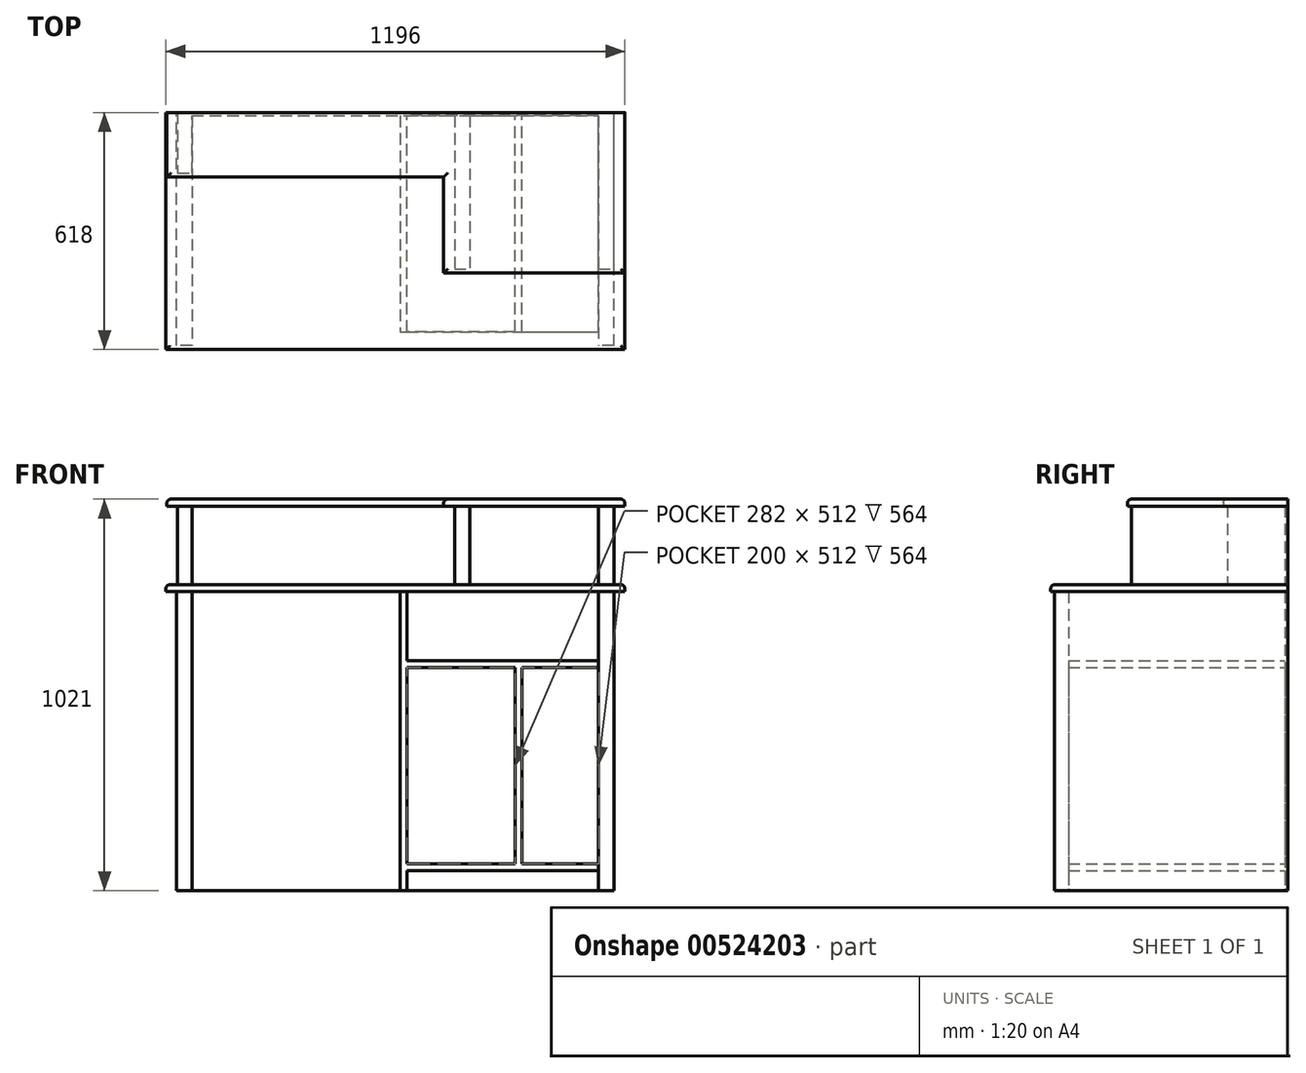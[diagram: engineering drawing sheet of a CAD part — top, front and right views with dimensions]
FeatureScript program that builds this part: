
annotation { "Feature Type Name" : "Feature", "Feature Type Description" : "" }
export const myFeature = defineFeature(function(context is Context, id is Id, definition is map)
    precondition{}
    {
        {
            var Q0;
            Q0=qCreatedBy(makeId("Top.planeOp"),FACE);
            var sketch = newSketch(context, id + "F0", { "sketchPlane" : qUnion([Q0])});
            skLineSegment(sketch, "E0.bottom", {"start": v(0, 0) * mm, "end": v(-1140, 0) * mm});
            skLineSegment(sketch, "E0.top", {"start": v(0, 608) * mm, "end": v(-1140, 608) * mm});
            skLineSegment(sketch, "E0.left", {"start": v(0, 0) * mm, "end": v(0, 608) * mm});
            skLineSegment(sketch, "E0.right", {"start": v(-1140, 0) * mm, "end": v(-1140, 608) * mm});
            skLineSegment(sketch, "E1.bottom", {"start": v(-1100, 600) * mm, "end": v(-40, 600) * mm});
            skLineSegment(sketch, "E1.top", {"start": v(-1100, 0) * mm, "end": v(-40, 0) * mm});
            skLineSegment(sketch, "E1.left", {"start": v(-1100, 600) * mm, "end": v(-1100, 0) * mm});
            skLineSegment(sketch, "E1.right", {"start": v(-40, 600) * mm, "end": v(-40, 0) * mm});
            skLineSegment(sketch, "E2.bottom", {"start": v(-558, 600) * mm, "end": v(-540, 600) * mm});
            skLineSegment(sketch, "E2.top", {"start": v(-558, 36) * mm, "end": v(-540, 36) * mm});
            skLineSegment(sketch, "E2.left", {"start": v(-558, 600) * mm, "end": v(-558, 36) * mm});
            skLineSegment(sketch, "E2.right", {"start": v(-540, 600) * mm, "end": v(-540, 36) * mm});
            skSolve(sketch);
        }
        {
            var Q0;
            Q0=makeQuery(id+"F0.imprint","IMPRINT",FACE,{"disambiguationData":[TD([[makeQuery(id+"F0.imprint","IMPRINT",EDGE,{"derivedFrom":sQuery(id+"F0.wireOp",EDGE,"E0.top")}),1.0]])]});
            var Q1;
            Q1=makeQuery(id+"F0.imprint","IMPRINT",FACE,{"disambiguationData":[TD([[makeQuery(id+"F0.imprint","IMPRINT",EDGE,{"derivedFrom":sQuery(id+"F0.wireOp",EDGE,"E2.top")}),1.0]])]});
            extrude(context, id + "F1", {"entities" : qUnion([Q0, Q1]), "depth" : 780 * mm, "offsetDistance" : 25 * mm});
        }
        {
            var Q0;
            {var subQ0=sQuery(id+"F0.wireOp",EDGE,"E1.bottom");Q0=makeQuery(id+"F1.opExtrude","SWEPT_FACE",FACE,{"disambiguationData":[OSD([subQ0]),TDD([makeQuery(id+"F0.imprint","IMPRINT",EDGE,{"disambiguationData":[TD([[makeQuery(id+"F0.imprint","INTERSECT",VERTEX,{"derivedFrom":[subQ0,sQuery(id+"F0.wireOp",EDGE,"E2.right")]}),-1.0]])],"derivedFrom":subQ0})])]});}
            var sketch = newSketch(context, id + "F2", { "sketchPlane" : qUnion([Q0])});
            skLineSegment(sketch, "E3.bottom", {"start": v(-540, 52) * mm, "end": v(-40, 52) * mm});
            skLineSegment(sketch, "E3.top", {"start": v(-540, 70) * mm, "end": v(-40, 70) * mm});
            skLineSegment(sketch, "E3.left", {"start": v(-540, 52) * mm, "end": v(-540, 70) * mm});
            skLineSegment(sketch, "E3.right", {"start": v(-40, 52) * mm, "end": v(-40, 70) * mm});
            skLineSegment(sketch, "E4.bottom", {"start": v(-40, 582) * mm, "end": v(-540, 582) * mm});
            skLineSegment(sketch, "E4.top", {"start": v(-40, 600) * mm, "end": v(-540, 600) * mm});
            skLineSegment(sketch, "E4.left", {"start": v(-40, 582) * mm, "end": v(-40, 600) * mm});
            skLineSegment(sketch, "E4.right", {"start": v(-540, 582) * mm, "end": v(-540, 600) * mm});
            skLineSegment(sketch, "E5.0", {"start": v(-1100, 780) * mm, "end": v(-558, 780) * mm});
            skLineSegment(sketch, "E6.bottom", {"start": v(-258, 582) * mm, "end": v(-240, 582) * mm});
            skLineSegment(sketch, "E6.top", {"start": v(-258, 70) * mm, "end": v(-240, 70) * mm});
            skLineSegment(sketch, "E6.left", {"start": v(-258, 582) * mm, "end": v(-258, 70) * mm});
            skLineSegment(sketch, "E6.right", {"start": v(-240, 582) * mm, "end": v(-240, 70) * mm});
            skSolve(sketch);
        }
        {
            var Q0;
            {var subQ0=sQuery(id+"F2.wireOp",EDGE,"E6.left");Q0=qUnion([makeQuery(id+"F2.imprint","IMPRINT",FACE,{"disambiguationData":[TD([[makeQuery(id+"F2.imprint","IMPRINT",EDGE,{"derivedFrom":sQuery(id+"F2.wireOp",EDGE,"E3.bottom")}),1.0]])]}),makeQuery(id+"F2.imprint","IMPRINT",FACE,{"disambiguationData":[TD([[makeQuery(id+"F2.imprint","IMPRINT",EDGE,{"derivedFrom":subQ0}),1.0]])]}),makeQuery(id+"F2.imprint","IMPRINT",FACE,{"disambiguationData":[TD([[makeQuery(id+"F2.imprint","IMPRINT",EDGE,{"derivedFrom":sQuery(id+"F2.wireOp",EDGE,"E4.top")}),1.0]])]})]);}
            extrude(context, id + "F3", {"entities" : qUnion([Q0]), "operationType" : NewBodyOperationType.ADD, "depth" : 564 * mm, "offsetDistance" : 25 * mm});
        }
        {
            var Q0;
            Q0=makeQuery(id+"F1.opExtrude","CAP_FACE",FACE,{"disambiguationData":[OSD([sQuery(id+"F0.wireOp",EDGE,"E0.bottom"),sQuery(id+"F0.wireOp",EDGE,"E0.top"),sQuery(id+"F0.wireOp",EDGE,"E0.left"),sQuery(id+"F0.wireOp",EDGE,"E0.right"),sQuery(id+"F0.wireOp",EDGE,"E1.bottom"),sQuery(id+"F0.wireOp",EDGE,"E1.left"),sQuery(id+"F0.wireOp",EDGE,"E1.right"),sQuery(id+"F0.wireOp",EDGE,"E2.top"),sQuery(id+"F0.wireOp",EDGE,"E2.left"),sQuery(id+"F0.wireOp",EDGE,"E2.right")])],"isStart":false});
            var sketch = newSketch(context, id + "F4", { "sketchPlane" : qUnion([Q0])});
            skLineSegment(sketch, "E7.0", {"start": v(0, 608) * mm, "end": v(-1140, 608) * mm});
            skLineSegment(sketch, "E8.0", {"start": v(-1140, 0) * mm, "end": v(-1140, 608) * mm});
            skLineSegment(sketch, "E9.0", {"start": v(0, 0) * mm, "end": v(0, 608) * mm});
            skLineSegment(sketch, "E10.0", {"start": v(-1100, 0) * mm, "end": v(-1140, 0) * mm});
            skLineSegment(sketch, "E11.0", {"start": v(0, 0) * mm, "end": v(-40, 0) * mm});
            skLineSegment(sketch, "E12.bottom", {"start": v(-1168, 608) * mm, "end": v(28, 608) * mm});
            skLineSegment(sketch, "E12.top", {"start": v(-1168, -10) * mm, "end": v(28, -10) * mm});
            skLineSegment(sketch, "E12.left", {"start": v(-1168, 608) * mm, "end": v(-1168, -10) * mm});
            skLineSegment(sketch, "E12.right", {"start": v(28, 608) * mm, "end": v(28, -10) * mm});
            skSolve(sketch);
        }
        {
            var Q0;
            {var subQ8=sQuery(id+"F4.wireOp",EDGE,"E7.0");var subQ10=sQuery(id+"F4.wireOp",EDGE,"E8.0");var subQ11=makeQuery(id+"F4.imprint","IMPRINT",EDGE,{"derivedFrom":subQ10});Q0=qUnion([makeQuery(id+"F4.imprint","IMPRINT",FACE,{"disambiguationData":[TD([[subQ11,1.0]])]}),makeQuery(id+"F4.imprint","IMPRINT",FACE,{"disambiguationData":[TD([[makeQuery(id+"F4.imprint","IMPRINT",EDGE,{"derivedFrom":subQ8}),1.0]])]})]);}
            extrude(context, id + "F5", {"entities" : qUnion([Q0]), "operationType" : NewBodyOperationType.ADD, "depth" : 18 * mm, "offsetDistance" : 25 * mm});
        }
        {
            var Q0;
            Q0=makeQuery(id+"F5.opExtrude","CAP_EDGE",EDGE,{"disambiguationData":[OSD([sQuery(id+"F4.wireOp",EDGE,"E12.top")])],"isStart":false});
            var Q1;
            Q1=makeQuery(id+"F5.opExtrude","CAP_EDGE",EDGE,{"disambiguationData":[OSD([sQuery(id+"F4.wireOp",EDGE,"E12.left")])],"isStart":false});
            var Q2;
            Q2=makeQuery(id+"F5.opExtrude","CAP_EDGE",EDGE,{"disambiguationData":[OSD([sQuery(id+"F4.wireOp",EDGE,"E12.right")])],"isStart":false});
            fillet(context, id + "F6", {"entities" : qUnion([Q0, Q1, Q2]), "radius" : 10 * mm, "tangentPropagation" : true, "allowEdgeOverflow" : false});
        }
        {
            var Q0;
            Q0=makeQuery(id+"F5.opExtrude","CAP_FACE",FACE,{"disambiguationData":[OSD([sQuery(id+"F4.wireOp",EDGE,"E7.0"),sQuery(id+"F4.wireOp",EDGE,"E12.bottom"),sQuery(id+"F4.wireOp",EDGE,"E12.top"),sQuery(id+"F4.wireOp",EDGE,"E12.left"),sQuery(id+"F4.wireOp",EDGE,"E12.right")])],"isStart":false});
            var sketch = newSketch(context, id + "F7", { "sketchPlane" : qUnion([Q0])});
            skLineSegment(sketch, "E13.0.0", {"start": v(0, 608) * mm, "end": v(-1158, 608) * mm});
            skLineSegment(sketch, "E13.0.1", {"start": v(-1158, 608) * mm, "end": v(-1158, 0) * mm});
            skLineSegment(sketch, "E13.0.2", {"start": v(-1158, 0) * mm, "end": v(18, 0) * mm});
            skLineSegment(sketch, "E13.0.3", {"start": v(18, 0) * mm, "end": v(18, 608) * mm});
            skLineSegment(sketch, "E14.bottom", {"start": v(-1137.47, 608) * mm, "end": v(18, 608) * mm});
            skLineSegment(sketch, "E14.top", {"start": v(-1137.47, 450) * mm, "end": v(0, 450) * mm});
            skLineSegment(sketch, "E14.left", {"start": v(-1137.47, 608) * mm, "end": v(-1137.47, 450) * mm});
            skLineSegment(sketch, "E15", {"start": v(0, 450) * mm, "end": v(0, 608) * mm});
            skLineSegment(sketch, "E16.bottom", {"start": v(-1137.47, 450) * mm, "end": v(-1100, 450) * mm});
            skLineSegment(sketch, "E16.top", {"start": v(-1137.47, 608) * mm, "end": v(-1100, 608) * mm});
            skLineSegment(sketch, "E16.left", {"start": v(-1137.47, 450) * mm, "end": v(-1137.47, 608) * mm});
            skLineSegment(sketch, "E16.right", {"start": v(-1100, 450) * mm, "end": v(-1100, 608) * mm});
            skLineSegment(sketch, "E17.bottom", {"start": v(0, 450) * mm, "end": v(-40, 450) * mm});
            skLineSegment(sketch, "E17.top", {"start": v(0, 608) * mm, "end": v(-40, 608) * mm});
            skLineSegment(sketch, "E17.right", {"start": v(-40, 450) * mm, "end": v(-40, 608) * mm});
            skPoint(sketch, "E18.oppositeSnap0", {"position": v(18, 304) * mm});
            skLineSegment(sketch, "E18.bottom", {"start": v(-40, 450) * mm, "end": v(0, 450) * mm});
            skLineSegment(sketch, "E18.left", {"start": v(-40, 450) * mm, "end": v(-40, 200) * mm});
            skLineSegment(sketch, "E18.right", {"start": v(0, 450) * mm, "end": v(0, 200) * mm});
            skLineSegment(sketch, "E19.0", {"start": v(-1100, 600) * mm, "end": v(-40, 600) * mm});
            skLineSegment(sketch, "E20.bottom", {"start": v(-415.9, 600) * mm, "end": v(-375.9, 600) * mm});
            skLineSegment(sketch, "E20.top", {"start": v(-415.9, 200) * mm, "end": v(-375.9, 200) * mm});
            skLineSegment(sketch, "E20.left", {"start": v(-415.9, 600) * mm, "end": v(-415.9, 200) * mm});
            skLineSegment(sketch, "E20.right", {"start": v(-375.9, 600) * mm, "end": v(-375.9, 200) * mm});
            skLineSegment(sketch, "E21", {"start": v(-40, 200) * mm, "end": v(0, 200) * mm});
            skPoint(sketch, "E22.orphan", {"position": v(0, 304) * mm});
            skSolve(sketch);
        }
        {
            var Q0;
            {var subQ4=sQuery(id+"F7.wireOp",EDGE,"E14.left");Q0=makeQuery(id+"F7.imprint","IMPRINT",FACE,{"disambiguationData":[TD([[makeQuery(id+"F7.imprint","IMPRINT",EDGE,{"derivedFrom":subQ4}),1.0]])]});}
            var Q1;
            {var subQ5=sQuery(id+"F7.wireOp",EDGE,"E20.top");Q1=makeQuery(id+"F7.imprint","IMPRINT",FACE,{"disambiguationData":[TD([[makeQuery(id+"F7.imprint","IMPRINT",EDGE,{"derivedFrom":subQ5}),1.0]])]});}
            var Q2;
            {var subQ0=sQuery(id+"F7.wireOp",EDGE,"E20.left");var subQ1=sQuery(id+"F7.wireOp",EDGE,"E14.top");var subQ2=makeQuery(id+"F7.imprint","INTERSECT",VERTEX,{"derivedFrom":[subQ1,subQ0]});Q2=makeQuery(id+"F7.imprint","IMPRINT",FACE,{"disambiguationData":[TD([[makeQuery(id+"F7.imprint","IMPRINT",EDGE,{"disambiguationData":[TD([[subQ2,-1.0]])],"derivedFrom":subQ1}),1.0]])]});}
            var Q3;
            {var subQ4=sQuery(id+"F7.wireOp",EDGE,"E15");Q3=makeQuery(id+"F7.imprint","IMPRINT",FACE,{"disambiguationData":[TD([[makeQuery(id+"F7.imprint","IMPRINT",EDGE,{"derivedFrom":subQ4}),1.0]])]});}
            var Q4;
            {var subQ2=sQuery(id+"F7.wireOp",EDGE,"E18.left");Q4=makeQuery(id+"F7.imprint","IMPRINT",FACE,{"disambiguationData":[TD([[makeQuery(id+"F7.imprint","IMPRINT",EDGE,{"derivedFrom":subQ2}),1.0]])]});}
            var Q5;
            {var subQ1=sQuery(id+"F7.wireOp",EDGE,"E13.0.0");var subQ5=sQuery(id+"F7.wireOp",EDGE,"E16.right");var subQ8=makeQuery(id+"F7.imprint","INTERSECT",VERTEX,{"derivedFrom":[subQ1,subQ5]});Q5=makeQuery(id+"F7.imprint","IMPRINT",FACE,{"disambiguationData":[TD([[makeQuery(id+"F7.imprint","IMPRINT",EDGE,{"disambiguationData":[TD([[subQ8,-1.0]])],"derivedFrom":subQ1}),-1.0]])]});}
            extrude(context, id + "F8", {"entities" : qUnion([Q0, Q1, Q2, Q3, Q4, Q5]), "operationType" : NewBodyOperationType.ADD, "depth" : 205 * mm, "offsetDistance" : 25 * mm});
        }
        {
            var Q0;
            Q0=makeQuery(id+"F8.opExtrude","CAP_FACE",FACE,{"disambiguationData":[OSD([sQuery(id+"F7.wireOp",EDGE,"E13.0.0"),sQuery(id+"F7.wireOp",EDGE,"E14.top"),sQuery(id+"F7.wireOp",EDGE,"E14.left"),sQuery(id+"F7.wireOp",EDGE,"E15"),sQuery(id+"F7.wireOp",EDGE,"E16.right"),sQuery(id+"F7.wireOp",EDGE,"E17.right"),sQuery(id+"F7.wireOp",EDGE,"E18.left"),sQuery(id+"F7.wireOp",EDGE,"E18.right"),sQuery(id+"F7.wireOp",EDGE,"E19.0"),sQuery(id+"F7.wireOp",EDGE,"E20.top"),sQuery(id+"F7.wireOp",EDGE,"E20.left"),sQuery(id+"F7.wireOp",EDGE,"E20.right"),sQuery(id+"F7.wireOp",EDGE,"E21")])],"isStart":false});
            var sketch = newSketch(context, id + "F9", { "sketchPlane" : qUnion([Q0])});
            skLineSegment(sketch, "E23.0", {"start": v(-1137.47, 608) * mm, "end": v(0, 608) * mm});
            skLineSegment(sketch, "E24.0", {"start": v(-1137.47, 450) * mm, "end": v(-1137.47, 608) * mm});
            skLineSegment(sketch, "E25.0", {"start": v(0, 200) * mm, "end": v(0, 608) * mm});
            skLineSegment(sketch, "E26.0", {"start": v(-1137.47, 450) * mm, "end": v(-1100, 450) * mm});
            skLineSegment(sketch, "E27.0", {"start": v(-415.9, 200) * mm, "end": v(-375.9, 200) * mm});
            skLineSegment(sketch, "E28.bottom", {"start": v(-1165.47, 608) * mm, "end": v(28, 608) * mm});
            skLineSegment(sketch, "E28.top", {"start": v(-443.9, 190) * mm, "end": v(28, 190) * mm});
            skLineSegment(sketch, "E28.left", {"start": v(-1165.47, 608) * mm, "end": v(-1165.47, 440) * mm});
            skLineSegment(sketch, "E28.right", {"start": v(28, 608) * mm, "end": v(28, 190) * mm});
            skLineSegment(sketch, "E29", {"start": v(-1165.47, 440) * mm, "end": v(-443.9, 440) * mm});
            skLineSegment(sketch, "E30", {"start": v(-443.9, 440) * mm, "end": v(-443.9, 190) * mm});
            skSolve(sketch);
        }
        {
            var Q0;
            {var subQ4=sQuery(id+"F9.wireOp",EDGE,"E23.0");var subQ5=sQuery(id+"F9.wireOp",EDGE,"E24.0");var subQ6=makeQuery(id+"F9.imprint","IMPRINT",EDGE,{"derivedFrom":subQ5});Q0=qUnion([makeQuery(id+"F9.imprint","IMPRINT",FACE,{"disambiguationData":[TD([[makeQuery(id+"F9.imprint","IMPRINT",EDGE,{"derivedFrom":subQ4}),-1.0]])]}),makeQuery(id+"F9.imprint","IMPRINT",FACE,{"disambiguationData":[TD([[subQ6,-1.0]])]})]);}
            extrude(context, id + "F10", {"entities" : qUnion([Q0]), "operationType" : NewBodyOperationType.ADD, "depth" : 18 * mm, "offsetDistance" : 25 * mm});
        }
        {
            var Q0;
            Q0=makeQuery(id+"F10.opExtrude","CAP_EDGE",EDGE,{"disambiguationData":[OSD([sQuery(id+"F9.wireOp",EDGE,"E28.left")])],"isStart":false});
            var Q1;
            Q1=makeQuery(id+"F10.opExtrude","CAP_EDGE",EDGE,{"disambiguationData":[OSD([sQuery(id+"F9.wireOp",EDGE,"E29")])],"isStart":false});
            var Q2;
            Q2=makeQuery(id+"F10.opExtrude","CAP_EDGE",EDGE,{"disambiguationData":[OSD([sQuery(id+"F9.wireOp",EDGE,"E30")])],"isStart":false});
            var Q3;
            Q3=makeQuery(id+"F10.opExtrude","CAP_EDGE",EDGE,{"disambiguationData":[OSD([sQuery(id+"F9.wireOp",EDGE,"E28.top")])],"isStart":false});
            var Q4;
            Q4=makeQuery(id+"F10.opExtrude","CAP_EDGE",EDGE,{"disambiguationData":[OSD([sQuery(id+"F9.wireOp",EDGE,"E28.right")])],"isStart":false});
            fillet(context, id + "F11", {"entities" : qUnion([Q0, Q1, Q2, Q3, Q4]), "radius" : 10 * mm, "tangentPropagation" : true, "allowEdgeOverflow" : false});
        }
    });
